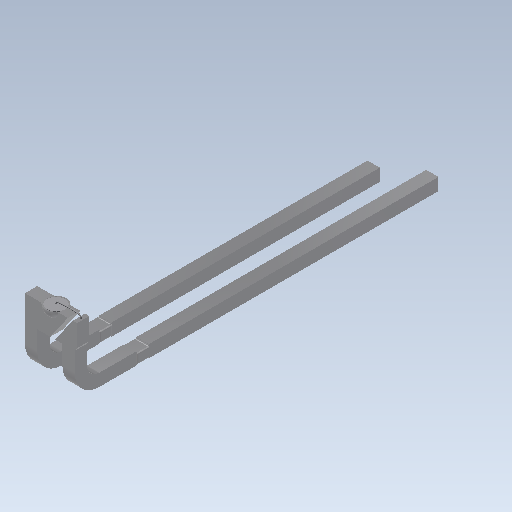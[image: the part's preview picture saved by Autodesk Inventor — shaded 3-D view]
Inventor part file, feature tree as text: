
AUTODESK INVENTOR PART (.ipt)
format: ipt  version: 2020.1 (Build 241239000, 239)  size: 350,720 bytes
history: native  units: mm
features: sketch x8, fillet x4, other x3, revolve x3, extrude x2, projected_geometry x2, sweep x1
ambient origin geometry x8: Origin, YZ Plane, XZ Plane, XY Plane, X Axis, Y Axis, Z Axis, Center Point
bodies: Body1 (feature_tree), Body2 (feature_tree)
feature tree (23):
  other  "Sólido1"
  extrude  "Extrusión1"  Depth=0.98mm
  extrude  "Extrusión2"  Depth=0.98mm
  fillet  "Empalme6"  Radius=4.0mm
  fillet  "Empalme7"  Radius=2.0mm
  fillet  "Empalme8"  Radius=1.0mm
  fillet  "Empalme9"  Radius=4.0mm
  revolve  "Revolución1"  [1 undecoded]
  revolve  "Revolución2"  [1 undecoded]
  revolve  "Revolución3"  [1 undecoded]
  sweep  "Barrido1"
  other  "Bend Part1"
  sketch  "Boceto1"  dims[d0=0.98mm d1=0.98mm]
  sketch  "Boceto2"  dims[d2=4.0mm d3=0.98mm d4=4.0mm d5=2.0mm d6=1.0mm d7=4.0mm]
  sketch  "Boceto3"  dims[d8=2.0mm d9=21.816616mm]
  sketch  "Boceto4"  dims[d10=9.599311mm d11=1.0mm]
  sketch  "Boceto5"  dims[d12=28.1mm d13=1.7mm]
  other  "Sólido2"
  sketch  "Boceto6"  dims[d14=0.98mm d15=0.0mm d16=1.18mm]
  projected_geometry  "Contorno proyectado1"
  projected_geometry  "Contorno proyectado2"
  sketch  "Boceto7"  dims[d17=1.18mm]
  sketch  "Sketch8"  dims[d20=0.1mm d21=0.1mm d22=0.78mm d23=0.0mm d29=0.1mm d30=0.1mm d31=0.1mm d32=0.1mm d33=180.0deg d34=180.0deg d35=180.0deg d36=0.1mm d37=0.0mm d38=0.0mm d40=1.0mm d41=90.0deg d46=3.5mm]
note: 3 required parameter values undecoded (feature->parameter linkage not recoverable at this tier; creation-order binding heuristic only, values carry confidence <= 0.55)
